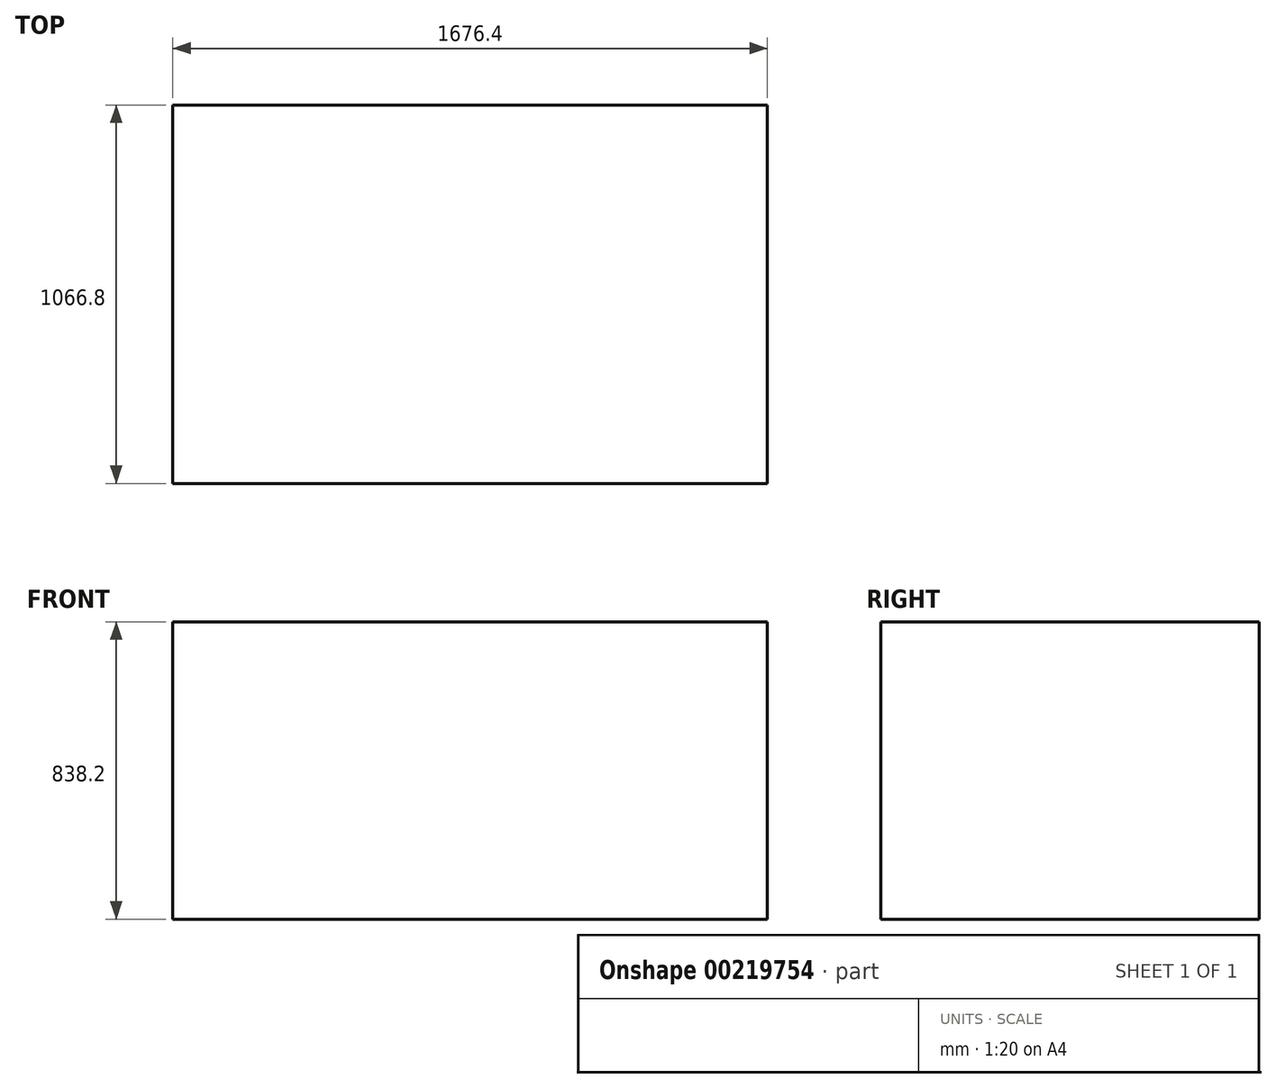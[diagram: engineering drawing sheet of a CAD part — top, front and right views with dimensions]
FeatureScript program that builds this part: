
annotation { "Feature Type Name" : "Feature", "Feature Type Description" : "" }
export const myFeature = defineFeature(function(context is Context, id is Id, definition is map)
    precondition{}
    {
        {
            var Q0;
            Q0=qCreatedBy(makeId("Top.planeOp"),FACE);
            var sketch = newSketch(context, id + "F0", { "sketchPlane" : qUnion([Q0])});
            skLineSegment(sketch, "E0.bottom", {"start": v(-838.2, 533.4) * mm, "end": v(838.2, 533.4) * mm});
            skLineSegment(sketch, "E0.top", {"start": v(-838.2, -533.4) * mm, "end": v(838.2, -533.4) * mm});
            skLineSegment(sketch, "E0.left", {"start": v(-838.2, 533.4) * mm, "end": v(-838.2, -533.4) * mm});
            skLineSegment(sketch, "E0.right", {"start": v(838.2, 533.4) * mm, "end": v(838.2, -533.4) * mm});
            skSolve(sketch);
        }
        {
            var Q0;
            Q0 = qSketchRegion(id + "F0", true);
            extrude(context, id + "F1", {"entities" : qUnion([Q0]), "depth" : 838.2 * mm});
        }
    });
